# Revit family: Capsule V 310-1600
name_source: partatom
category: Оборудование
units: mm (PartAtom-declared; Revit-internal decimal feet)

## family parameters
Всегда вертикально = Да
Классификация = Нет
На основе рабочей плоскости = Нет
Общий = Нет
При загрузке вырезать с полостями = Нет
Размер круглого соединителя = Использовать диаметр
Тип детали = Нормальный
Точка расчета площади = Нет

## types (4) — shared parameters
ADSK_Единица измерения = шт.
ADSK_Завод-изготовитель = ООО «Турков»
ADSK_Количество = 1
ADSK_Количество фаз = 1
ADSK_Наименование = Компактная вытяжная установка
ADSK_Напряжение = 220 В
ADSK_Ток = 1 А
В_крепежа = 10 мм
Высота_вв = 27 мм
Крепеж Y = 23 мм
Толщина крышки = 31 мм

## per-type parameters (varying)
| type | 600+ | A ширина | ADSK_Масса | ADSK_Номинальная мощность | ADSK_Расход воздуха приточный | ADSK_Свободный напор воздуха | B высота | Dn | ВВ_от_н_кр | Защелка X | Защелка_от_оси | Крепеж X | С глубина | СЗ_фильтры | угол |
| VBox 590 | Да | 550 мм | 40 | 160 Вт | 510.0 м³/ч | 539.0 Па | 452 мм | 200 мм | 165 мм | 61 мм | 28 мм | 52 мм | 280 мм | 300 мм | 15.11° |
| VBox 400 | Да | 590 мм | 35 | 105 Вт | 310.0 м³/ч | 490.0 Па | 410 мм | 160 мм | 150 мм | 65 мм | 12 мм | 7 мм | 250 мм | 250 мм | 18.65° |
| VBox 1100 | Нет | 528 мм | 60 | 165 Вт | 1100.0 м³/ч | 140.0 Па | 556 мм | 250 мм | 225 мм | 61 мм | 28 мм | 52 мм | 387 мм | 300 мм | 12.19° |
| VBox 1600 | Нет | 528 мм | 70 | 330 Вт | 1600.0 м³/ч | 306.0 Па | 656 мм | 315 мм | 250 мм | 61 мм | 28 мм | 52 мм | 437 мм | 300 мм | 9.73° |

note: column(s) folded — value = type name in every type: ADSK_Марка
